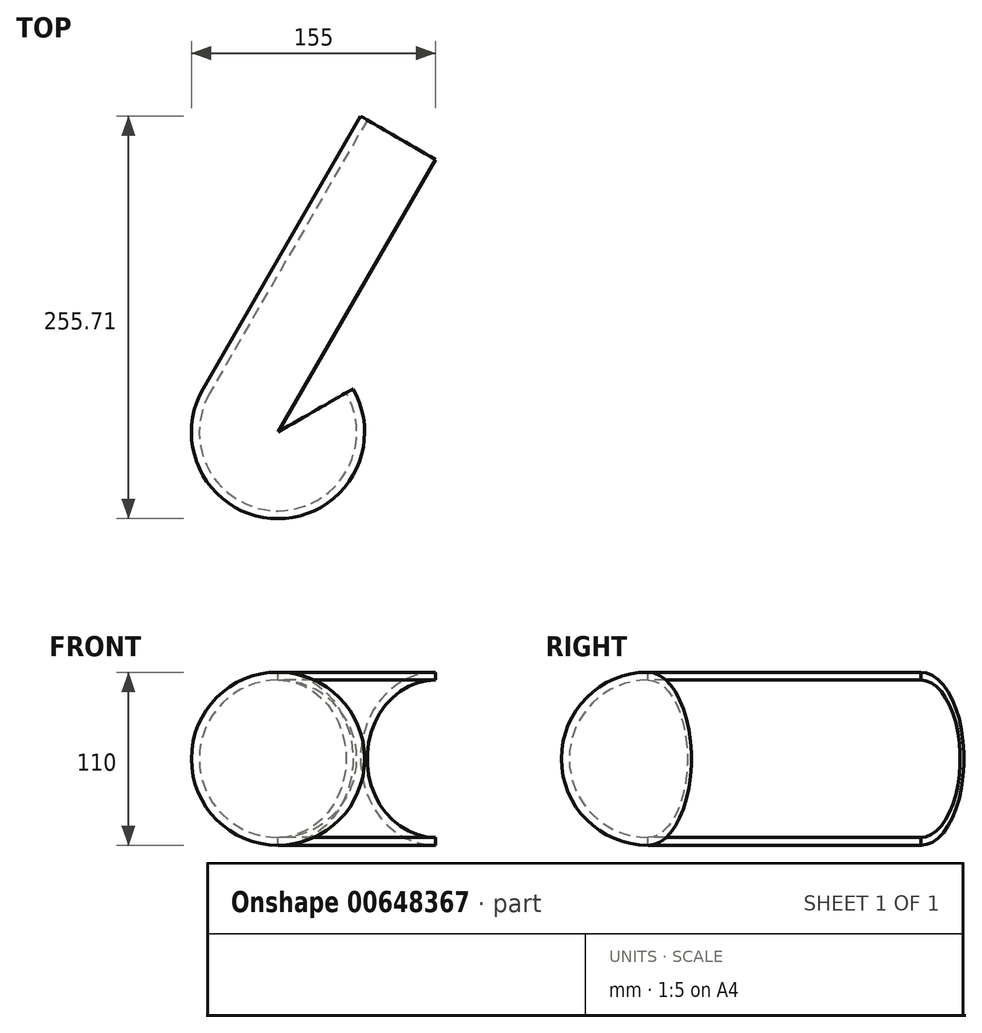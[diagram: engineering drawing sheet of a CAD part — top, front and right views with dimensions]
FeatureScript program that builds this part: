
annotation { "Feature Type Name" : "Feature", "Feature Type Description" : "" }
export const myFeature = defineFeature(function(context is Context, id is Id, definition is map)
    precondition{}
    {
        {
            var Q0;
            Q0=qCreatedBy(makeId("Right.planeOp"),FACE);
            var sketch = newSketch(context, id + "F0", { "sketchPlane" : qUnion([Q0])});
            skArc(sketch, "E0", {"start": v(0, 110) * mm, "mid": v(-55, 55) * mm, "end": v(0, 0) * mm});
            skArc(sketch, "E1", {"start": v(0, 105) * mm, "mid": v(-50, 55) * mm, "end": v(0, 5) * mm});
            skLineSegment(sketch, "E2", {"start": v(0, 0) * mm, "end": v(0, 5) * mm});
            skLineSegment(sketch, "E3", {"start": v(0, 105) * mm, "end": v(0, 110) * mm});
            skSolve(sketch);
        }
        {
            var Q0;
            Q0 = qSketchRegion(id + "F0", true);
            var Q1;
            Q1=sQuery(id+"F0.wireOp",EDGE,"E3");
            revolve(context, id + "F1", {"entities" : qUnion([Q0]), "axis" : qUnion([Q1]), "revolveType" : RevolveType.SYMMETRIC, "angle" : 240 * degree});
        }
        {
            var Q0;
            Q0=makeQuery(id+"F1.opRevolve","CAP_FACE",FACE,{"disambiguationData":[OSD([sQuery(id+"F0.wireOp",EDGE,"E0"),sQuery(id+"F0.wireOp",EDGE,"E1"),sQuery(id+"F0.wireOp",EDGE,"E2"),sQuery(id+"F0.wireOp",EDGE,"E3")])],"isStart":true});
            var sketch = newSketch(context, id + "F2", { "sketchPlane" : qUnion([Q0])});
            skSolve(sketch);
        }
        {
            var Q0;
            Q0=makeQuery(id+"F2.imprint","IMPRINT",FACE,{"disambiguationData":[TD([[makeQuery(id+"F2.imprint","IMPRINT",EDGE,{"derivedFrom":makeQuery(id+"F1.opRevolve","CAP_EDGE",EDGE,{"disambiguationData":[OSD([sQuery(id+"F0.wireOp",EDGE,"E0")])],"isStart":true})}),-1.0]])]});
            extrude(context, id + "F3", {"entities" : qUnion([Q0]), "operationType" : NewBodyOperationType.ADD, "depth" : 200 * mm, "offsetDistance" : 25 * mm});
        }
    });
